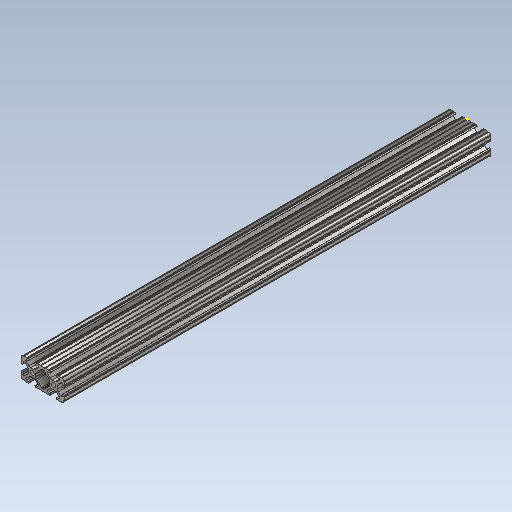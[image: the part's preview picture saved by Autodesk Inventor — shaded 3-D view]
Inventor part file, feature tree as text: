
AUTODESK INVENTOR PART (.ipt)
format: ipt  version: 2020 (Build 240168000, 168)  size: 343,040 bytes
history: native  units: in
note: dims shown in document units (in); Inventor stores cm internally (conversion verified against a paired STEP export)
features: sketch x2, extrude x1
ambient origin geometry x8: Origin, YZ Plane, XZ Plane, XY Plane, X Axis, Y Axis, Z Axis, Center Point
bodies: Solid1 (feature_tree)
feature tree (3):
  extrude  "Extrusion1"  [1 undecoded]
  sketch  "Sketch2"
  sketch  "Sketch1"  dims[d0=20.0in d1=0.0in]
note: 1 required parameter value undecoded (feature->parameter linkage not recoverable at this tier; creation-order binding heuristic only, values carry confidence <= 0.55)
